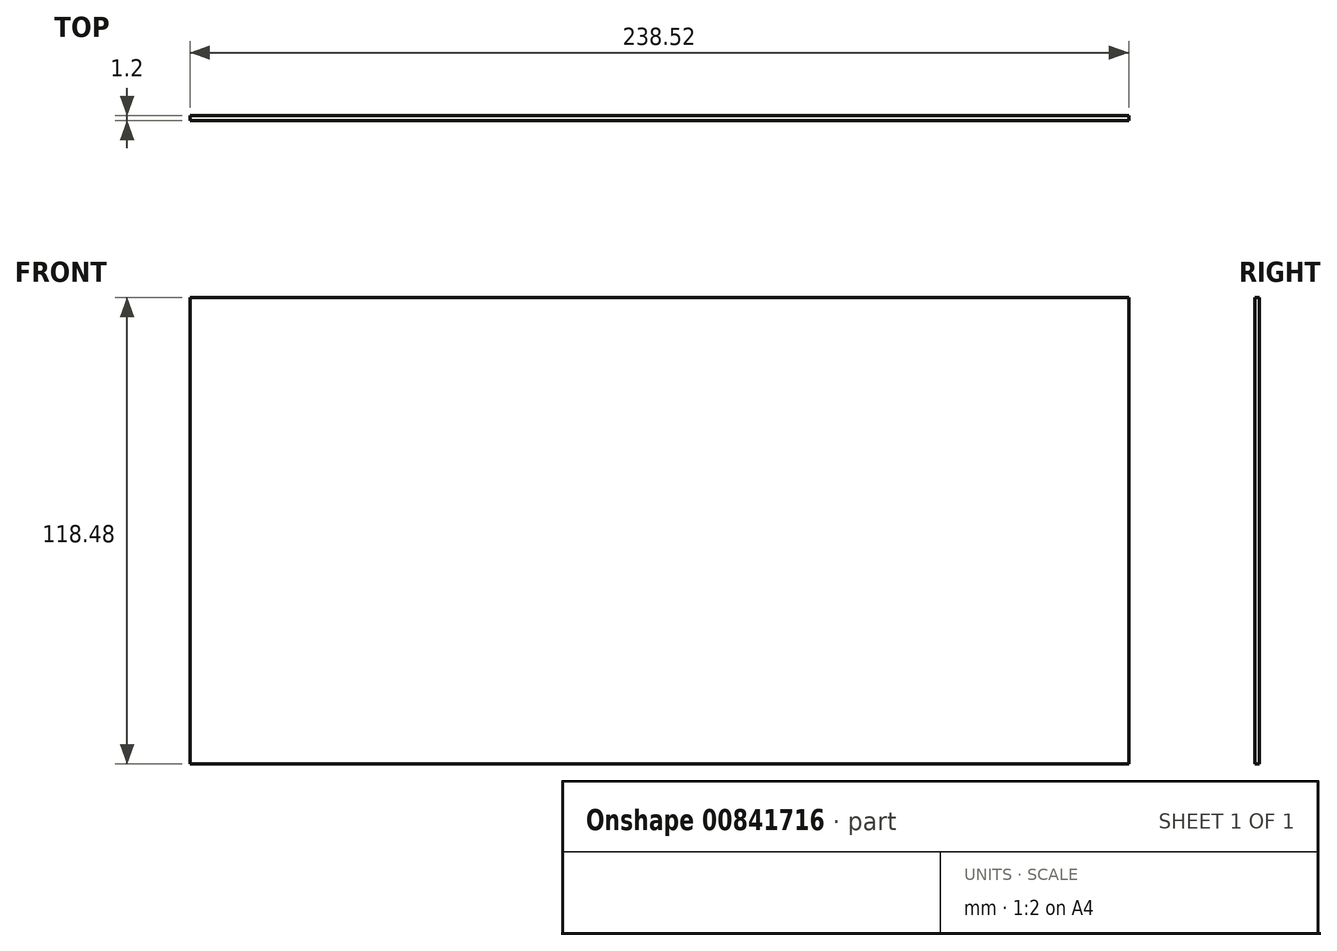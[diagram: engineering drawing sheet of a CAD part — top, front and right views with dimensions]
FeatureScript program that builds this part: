
annotation { "Feature Type Name" : "Feature", "Feature Type Description" : "" }
export const myFeature = defineFeature(function(context is Context, id is Id, definition is map)
    precondition{}
    {
        {
            var Q0;
            Q0=qCreatedBy(makeId("Front.planeOp"),FACE);
            var sketch = newSketch(context, id + "F0", { "sketchPlane" : qUnion([Q0])});
            skLineSegment(sketch, "E0.bottom", {"start": v(119.26, 59.24) * mm, "end": v(-119.26, 59.24) * mm});
            skLineSegment(sketch, "E0.top", {"start": v(119.26, -59.24) * mm, "end": v(-119.26, -59.24) * mm});
            skLineSegment(sketch, "E0.left", {"start": v(119.26, 59.24) * mm, "end": v(119.26, -59.24) * mm});
            skLineSegment(sketch, "E0.right", {"start": v(-119.26, 59.24) * mm, "end": v(-119.26, -59.24) * mm});
            skPoint(sketch, "E0.middle", {"position": v(0, 0) * mm});
            skSolve(sketch);
        }
        {
            var Q0;
            Q0=makeQuery(id+"F0.imprint","IMPRINT",FACE,{"disambiguationData":[TD([[makeQuery(id+"F0.imprint","IMPRINT",EDGE,{"derivedFrom":sQuery(id+"F0.wireOp",EDGE,"E0.bottom")}),1.0]])]});
            extrude(context, id + "F1", {"entities" : qUnion([Q0]), "depth" : 1.2 * mm, "offsetDistance" : 25.4 * mm});
        }
    });
